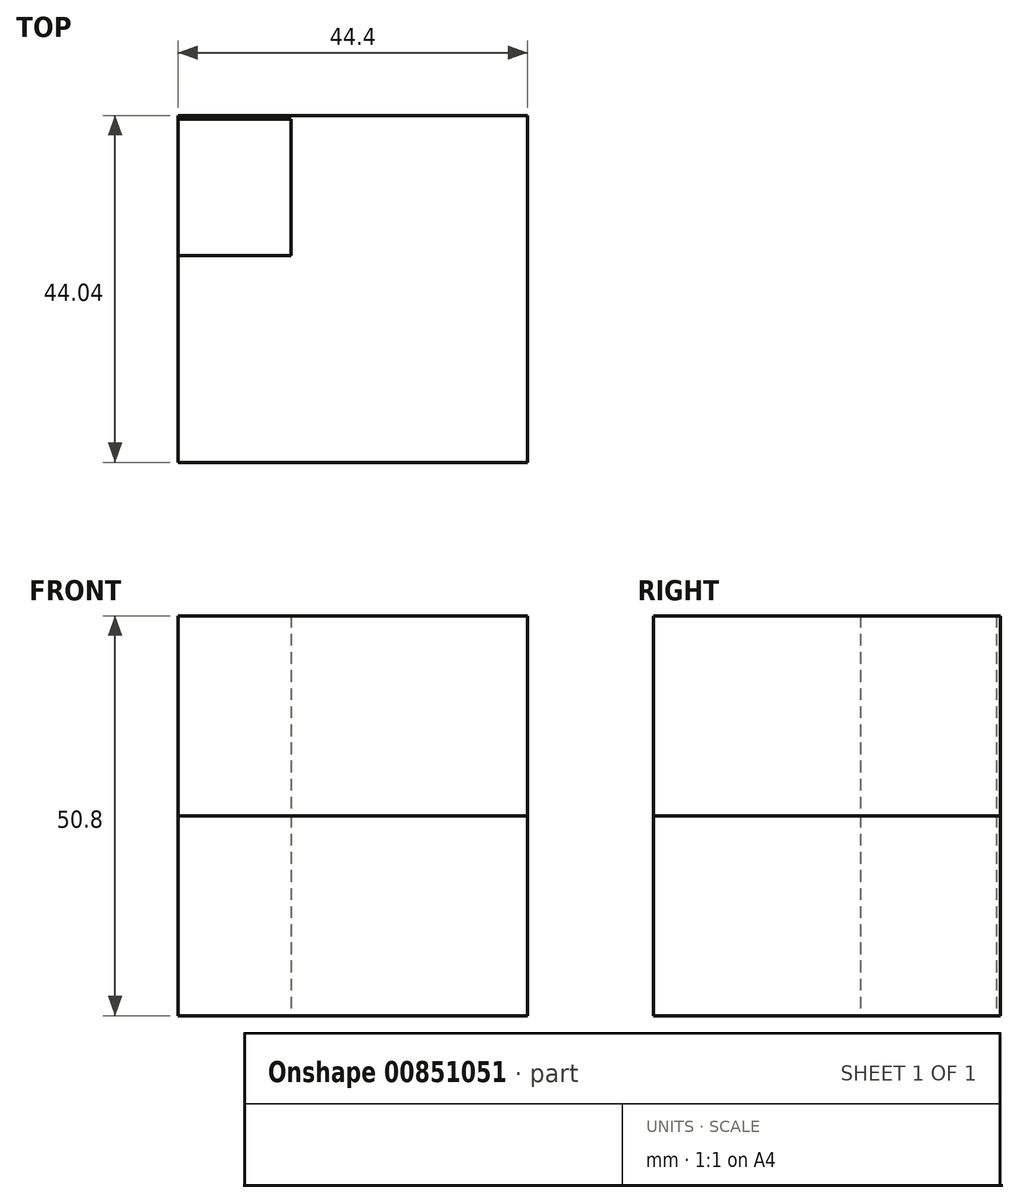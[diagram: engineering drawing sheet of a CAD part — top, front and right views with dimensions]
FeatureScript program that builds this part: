
annotation { "Feature Type Name" : "Feature", "Feature Type Description" : "" }
export const myFeature = defineFeature(function(context is Context, id is Id, definition is map)
    precondition{}
    {
        {
            var Q0;
            Q0=qCreatedBy(makeId("Top.planeOp"),FACE);
            var sketch = newSketch(context, id + "F0", { "sketchPlane" : qUnion([Q0])});
            skLineSegment(sketch, "E0.bottom", {"start": v(0, 44.04) * mm, "end": v(44.4, 44.04) * mm});
            skLineSegment(sketch, "E0.top", {"start": v(0, 0) * mm, "end": v(44.4, 0) * mm});
            skLineSegment(sketch, "E0.left", {"start": v(0, 44.04) * mm, "end": v(0, 0) * mm});
            skLineSegment(sketch, "E0.right", {"start": v(44.4, 44.04) * mm, "end": v(44.4, 0) * mm});
            skSolve(sketch);
        }
        {
            var Q0;
            Q0=makeQuery(id+"F0.imprint","IMPRINT",FACE,{"disambiguationData":[TD([[makeQuery(id+"F0.imprint","IMPRINT",EDGE,{"derivedFrom":sQuery(id+"F0.wireOp",EDGE,"E0.bottom")}),-1.0]])]});
            var sketch = newSketch(context, id + "F1", { "sketchPlane" : qUnion([Q0])});
            skLineSegment(sketch, "E1.bottom", {"start": v(0, 41.54) * mm, "end": v(0, 41.54) * mm});
            skLineSegment(sketch, "E1.top", {"start": v(0, 43.57) * mm, "end": v(0, 43.57) * mm});
            skLineSegment(sketch, "E1.left", {"start": v(0, 41.54) * mm, "end": v(0, 43.57) * mm});
            skLineSegment(sketch, "E1.right", {"start": v(0, 41.54) * mm, "end": v(0, 43.57) * mm});
            skLineSegment(sketch, "E2.bottom", {"start": v(14.34, 26.27) * mm, "end": v(0, 26.27) * mm});
            skLineSegment(sketch, "E2.top", {"start": v(14.34, 43.57) * mm, "end": v(0, 43.57) * mm});
            skLineSegment(sketch, "E2.left", {"start": v(14.34, 26.27) * mm, "end": v(14.34, 43.57) * mm});
            skLineSegment(sketch, "E2.right", {"start": v(0, 26.27) * mm, "end": v(0, 43.57) * mm});
            skSolve(sketch);
        }
        {
            var Q0;
            Q0=makeQuery(id+"F0.imprint","IMPRINT",FACE,{"disambiguationData":[TD([[makeQuery(id+"F0.imprint","IMPRINT",EDGE,{"derivedFrom":sQuery(id+"F0.wireOp",EDGE,"E0.bottom")}),-1.0]])]});
            var Q1;
            {var subQ0=sQuery(id+"F1.wireOp",EDGE,"E2.bottom");Q1=makeQuery(id+"F1.imprint","IMPRINT",FACE,{"disambiguationData":[TD([[makeQuery(id+"F1.imprint","IMPRINT",EDGE,{"derivedFrom":subQ0}),-1.0]])]});}
            extrude(context, id + "F2", {"entities" : qUnion([Q0, Q1]), "depth" : 25.4 * mm, "offsetDistance" : 25.4 * mm});
        }
        {
            var Q0;
            Q0=makeQuery(id+"F2.opExtrude","CAP_FACE",FACE,{"disambiguationData":[OSD([sQuery(id+"F0.wireOp",EDGE,"E0.bottom"),sQuery(id+"F0.wireOp",EDGE,"E0.top"),sQuery(id+"F0.wireOp",EDGE,"E0.left"),sQuery(id+"F0.wireOp",EDGE,"E0.right")])],"isStart":false});
            var Q1;
            Q1=makeQuery(id+"F2.opExtrude","CAP_FACE",FACE,{"disambiguationData":[OSD([sQuery(id+"F1.wireOp",EDGE,"E2.bottom"),sQuery(id+"F1.wireOp",EDGE,"E2.top"),sQuery(id+"F1.wireOp",EDGE,"E2.left"),sQuery(id+"F1.wireOp",EDGE,"E2.right")])],"isStart":false});
            extrude(context, id + "F3", {"entities" : qUnion([Q0, Q1]), "depth" : 25.4 * mm, "offsetDistance" : 25.4 * mm});
        }
    });
